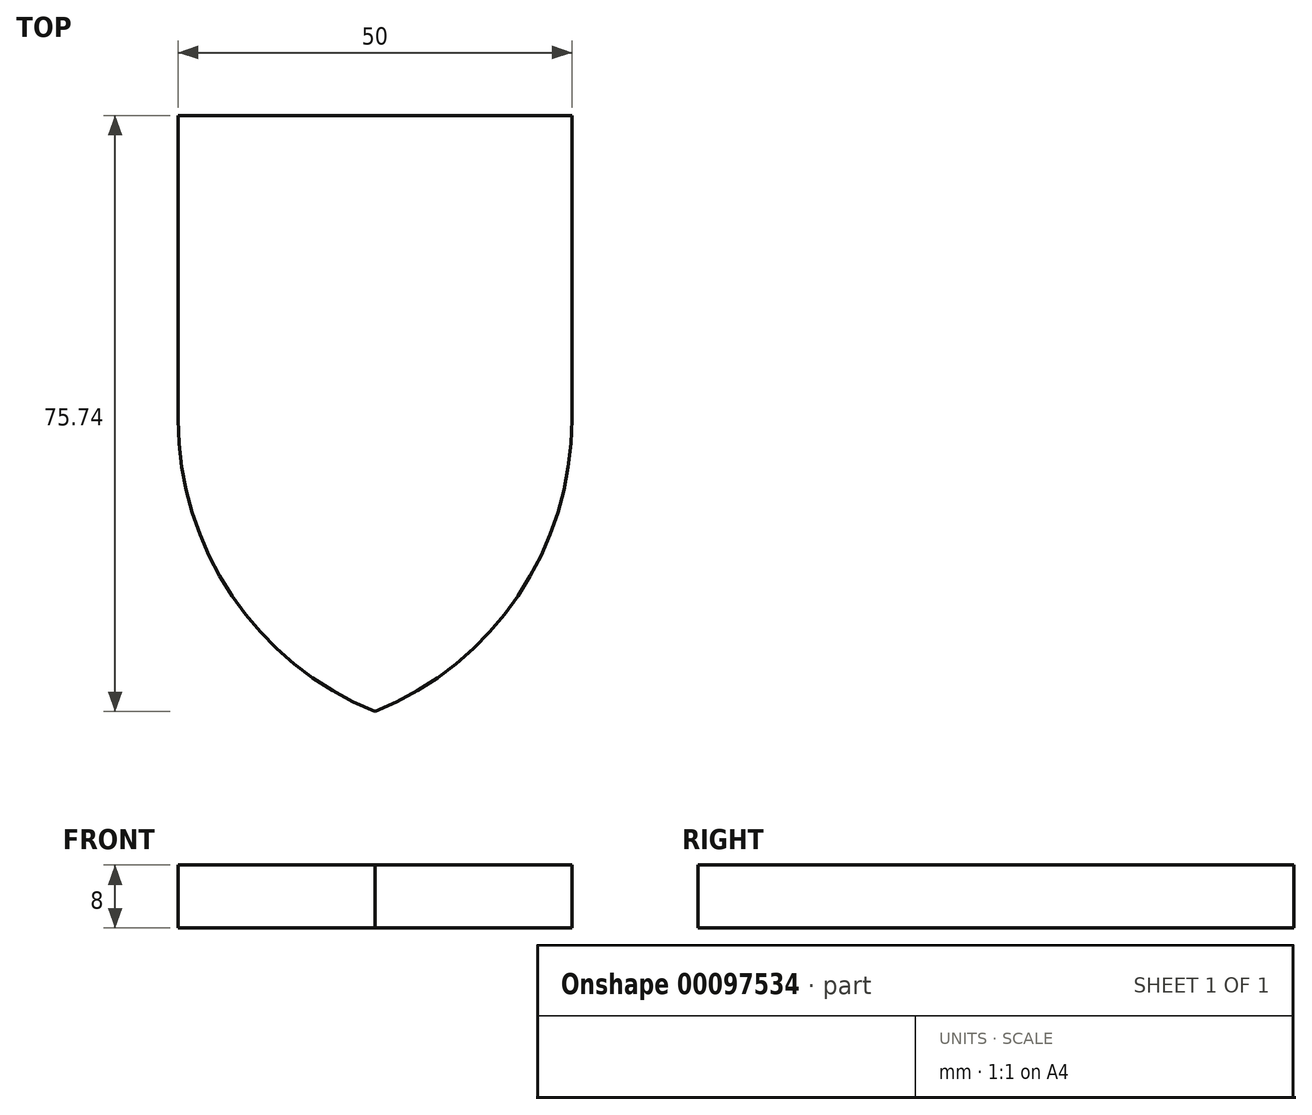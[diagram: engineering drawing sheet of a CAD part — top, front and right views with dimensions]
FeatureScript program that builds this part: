
annotation { "Feature Type Name" : "Feature", "Feature Type Description" : "" }
export const myFeature = defineFeature(function(context is Context, id is Id, definition is map)
    precondition{}
    {
        {
            var Q0;
            Q0=qCreatedBy(makeId("Top.planeOp"),FACE);
            var sketch = newSketch(context, id + "F0", { "sketchPlane" : qUnion([Q0])});
            skLineSegment(sketch, "E0.bottom", {"start": v(-25, 38.66) * mm, "end": v(25, 38.66) * mm});
            skArc(sketch, "E1", {"start": v(-25, 0) * mm, "mid": v(-18.17, -22.36) * mm, "end": v(0, -37.08) * mm});
            skArc(sketch, "E2", {"start": v(0, -37.08) * mm, "mid": v(18.17, -22.36) * mm, "end": v(25, 0) * mm});
            skLineSegment(sketch, "E3", {"start": v(-25, 38.66) * mm, "end": v(-25, 0) * mm});
            skLineSegment(sketch, "E4", {"start": v(25, 38.66) * mm, "end": v(25, 0) * mm});
            skSolve(sketch);
        }
        {
            var Q0;
            Q0=makeQuery(id+"F0.imprint","IMPRINT",FACE,{"disambiguationData":[TD([[makeQuery(id+"F0.imprint","IMPRINT",EDGE,{"derivedFrom":sQuery(id+"F0.wireOp",EDGE,"E0.bottom")}),-1.0]])]});
            extrude(context, id + "F1", {"entities" : qUnion([Q0]), "depth" : 8 * mm});
        }
    });
